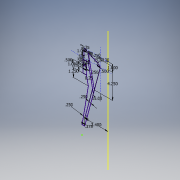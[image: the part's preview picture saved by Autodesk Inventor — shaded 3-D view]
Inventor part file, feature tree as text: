
AUTODESK INVENTOR PART (.ipt)
format: ipt  version: 2017 SP1 (Build 210196100, 196)  size: 127,488 bytes
history: native  units: in
note: dims shown in document units (in); Inventor stores cm internally (conversion verified against a paired STEP export)
features: sketch x1
ambient origin geometry x8: Origin, YZ Plane, XZ Plane, XY Plane, X Axis, Y Axis, Z Axis, Center Point
feature tree (1):
  sketch  "Sketch1"  dims[d0=1.13in d3=0.1718in d5=1.0in d6=1.0in d7=90.0deg d8=0.5in d9=15.0deg d31=0.25in d34=15.0deg d37=1.75in d40=3.75in d41=0.125in d46=0.75in d47=0.5in d51=0.5in d52=0.25in d54=0.5in d55=0.5in d56=1.25in d58=0.0017in d59=0.5in d60=0.5in d61=1.0in d62=0.234in d63=0.234in d64=0.125in d67=0.25in d68=4.25in d69=0.25in d70=0.25in d71=0.375in d73=3.4in d74=1.25in d75=0.2498in]
